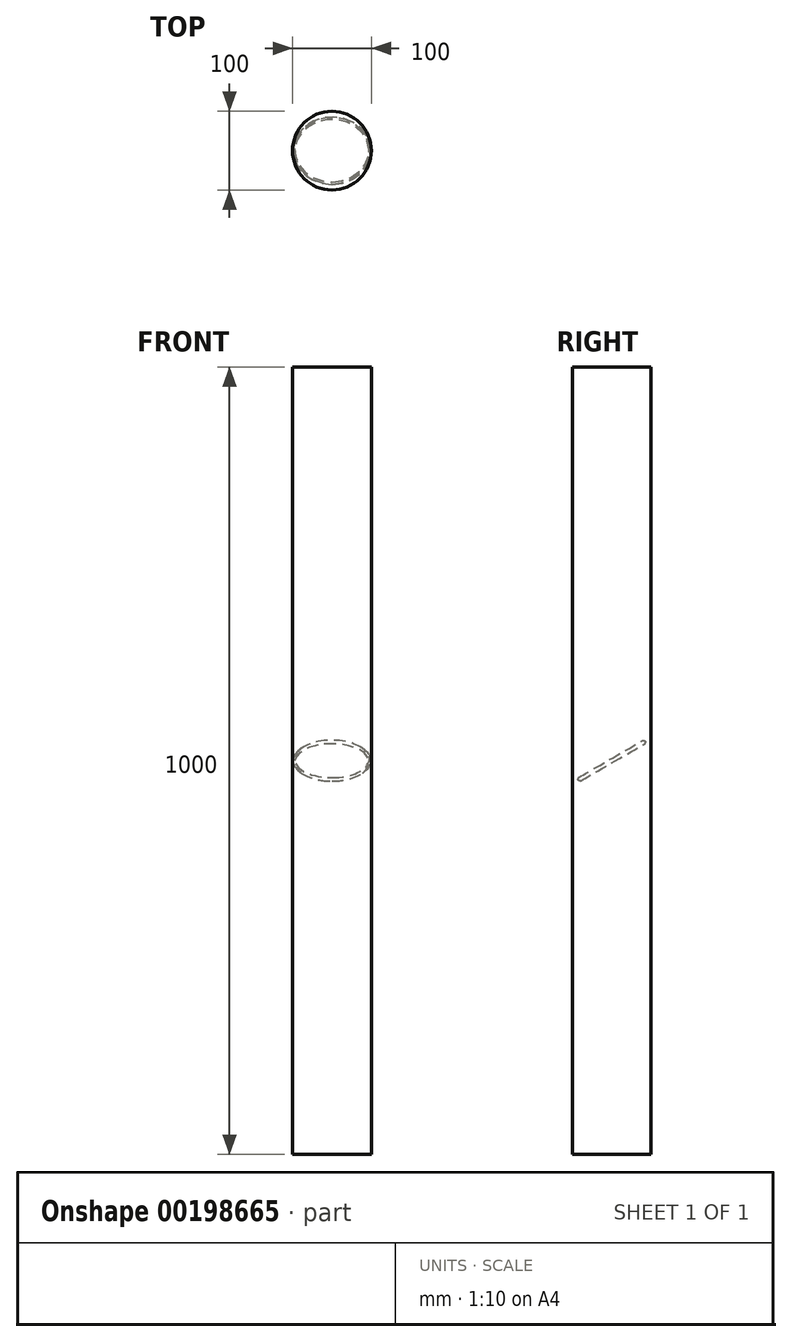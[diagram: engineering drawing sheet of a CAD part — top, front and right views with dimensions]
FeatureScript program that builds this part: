
annotation { "Feature Type Name" : "Feature", "Feature Type Description" : "" }
export const myFeature = defineFeature(function(context is Context, id is Id, definition is map)
    precondition{}
    {
        {
            var Q0;
            Q0=qCreatedBy(makeId("Top.planeOp"),FACE);
            var sketch = newSketch(context, id + "F0", { "sketchPlane" : qUnion([Q0])});
            skCircle(sketch, "E0", {"center": v(0, 0) * mm, "radius": 50 * mm});
            skSolve(sketch);
        }
        {
            var Q0;
            Q0 = qSketchRegion(id + "F0", true);
            var Q1;
            Q1=sQuery(id+"F0.wireOp",EDGE,"E0");
            extrude(context, id + "F1", {"entities" : qUnion([Q0]), "surfaceEntities" : qUnion([Q1]), "endBound" : BoundingType.SYMMETRIC, "depth" : 5 * mm});
        }
        {
            var Q0;
            Q0=qCreatedBy(makeId("Top.planeOp"),FACE);
            var sketch = newSketch(context, id + "F2", { "sketchPlane" : qUnion([Q0])});
            skLineSegment(sketch, "E1", {"start": v(-75.72, 0) * mm, "end": v(75.22, 0) * mm});
            skSolve(sketch);
        }
        {
            var Q0;
            Q0=makeQuery(id+"F1.opExtrude","SWEPT_BODY",BODY,{"disambiguationData":[OSD([sQuery(id+"F0.wireOp",EDGE,"E0")])]});
            var Q1;
            Q1=sQuery(id+"F2.wireOp",EDGE,"E1");
            transform(context, id + "F3", {"entities" : qUnion([Q0]), "transformType" : TransformType.ROTATION, "transformAxis" : qUnion([Q1]), "angle" : 30 * degree, "makeCopy" : false});
        }
        {
            var Q0;
            Q0=makeQuery(id+"F1.opExtrude","CAP_EDGE",EDGE,{"disambiguationData":[OSD([sQuery(id+"F0.wireOp",EDGE,"E0")])],"isStart":false});
            var Q1;
            Q1=makeQuery(id+"F1.opExtrude","CAP_EDGE",EDGE,{"disambiguationData":[OSD([sQuery(id+"F0.wireOp",EDGE,"E0")])],"isStart":true});
            chamfer(context, id + "F4", {"entities" : qUnion([Q0, Q1]), "width" : 2.5 * mm, "tangentPropagation" : true});
        }
        {
            var Q0;
            {var subQ0=sQuery(id+"F0.wireOp",EDGE,"E0");Q0=makeQuery(id+"F4.opChamfer","BLEND_EDGE",EDGE,{"blendedFrom":[makeQuery(id+"F1.opExtrude","CAP_EDGE",EDGE,{"disambiguationData":[OSD([subQ0])],"isStart":true}),makeQuery(id+"F1.opExtrude","CAP_EDGE",EDGE,{"disambiguationData":[OSD([subQ0])],"isStart":false})],"blendedInto":[]});}
            fillet(context, id + "F5", {"entities" : qUnion([Q0]), "radius" : 2 * mm, "tangentPropagation" : true, "allowEdgeOverflow" : false});
        }
        {
            var Q0;
            Q0=makeQuery(id+"F0.imprint","IMPRINT",FACE,{"disambiguationData":[TD([[makeQuery(id+"F0.imprint","IMPRINT",EDGE,{"derivedFrom":sQuery(id+"F0.wireOp",EDGE,"E0")}),1.0]])]});
            extrude(context, id + "F6", {"entities" : qUnion([Q0]), "endBound" : BoundingType.SYMMETRIC, "depth" : 1000 * mm});
        }
        {
            var Q0;
            Q0=makeQuery(id+"F1.opExtrude","SWEPT_BODY",BODY,{"disambiguationData":[OSD([sQuery(id+"F0.wireOp",EDGE,"E0")])]});
            var Q1;
            Q1=makeQuery(id+"F6.opExtrude","SWEPT_BODY",BODY,{"disambiguationData":[OSD([sQuery(id+"F0.wireOp",EDGE,"E0")])]});
            booleanBodies(context, id + "F7", {"operationType" : BooleanOperationType.SUBTRACTION, "tools" : qUnion([Q0]), "targets" : qUnion([Q1]), "keepTools" : true});
        }
    });
